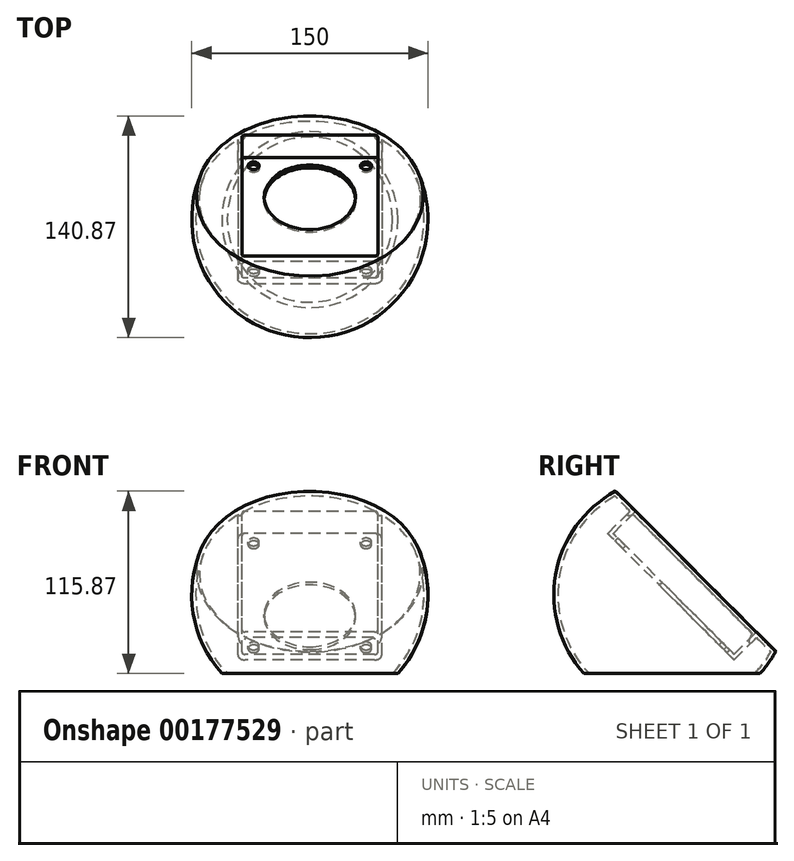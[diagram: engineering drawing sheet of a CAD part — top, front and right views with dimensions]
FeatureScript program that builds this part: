
annotation { "Feature Type Name" : "Feature", "Feature Type Description" : "" }
export const myFeature = defineFeature(function(context is Context, id is Id, definition is map)
    precondition{}
    {
        {
            var Q0;
            Q0=qCreatedBy(makeId("Front.planeOp"),FACE);
            var sketch = newSketch(context, id + "F0", { "sketchPlane" : qUnion([Q0])});
            skArc(sketch, "E0", {"start": v(55.9, 0) * mm, "mid": v(68.47, 80.62) * mm, "end": v(0, 125) * mm});
            skLineSegment(sketch, "E1", {"start": v(0, 0) * mm, "end": v(55.9, 0) * mm});
            skLineSegment(sketch, "E2", {"start": v(0, 50) * mm, "end": v(0, 0) * mm, "construction": true});
            skLineSegment(sketch, "E3", {"start": v(0, 0) * mm, "end": v(0, 125) * mm});
            skPoint(sketch, "E4.orphan", {"position": v(-55.9, 0) * mm});
            skSolve(sketch);
        }
        {
            var Q0;
            Q0=makeQuery(id+"F0.imprint","IMPRINT",FACE,{"disambiguationData":[TD([[makeQuery(id+"F0.imprint","IMPRINT",EDGE,{"derivedFrom":sQuery(id+"F0.wireOp",EDGE,"E0")}),1.0]])]});
            var Q1;
            Q1=sQuery(id+"F0.wireOp",EDGE,"E2");
            revolve(context, id + "F1", {"entities" : qUnion([Q0]), "axis" : qUnion([Q1]), "revolveType" : RevolveType.FULL});
        }
        {
            var Q0;
            Q0=makeQuery(id+"F1.opRevolve","SWEPT_FACE",FACE,{"disambiguationData":[OSD([sQuery(id+"F0.wireOp",EDGE,"E1")])]});
            var sketch = newSketch(context, id + "F2", { "sketchPlane" : qUnion([Q0])});
            skLineSegment(sketch, "E5", {"start": v(74.71, -80) * mm, "end": v(-64.99, -80) * mm, "construction": true});
            skSolve(sketch);
        }
        {
            var Q0;
            Q0=sQuery(id+"F2.wireOp",EDGE,"E5");
            cPlane(context, id + "F3", {"entities" : qUnion([Q0]), "cplaneType" : CPlaneType.LINE_ANGLE, "offset" : 25 * mm, "angle" : 45 * degree, "oppositeDirection" : true, "width" : 150 * mm, "height" : 150 * mm});
        }
        {
            var Q0;
            Q0=qCreatedBy(id+"F3.planeOp",FACE);
            var sketch = newSketch(context, id + "F4", { "sketchPlane" : qUnion([Q0])});
            skLineSegment(sketch, "E6.bottom", {"start": v(-80.9, 121.62) * mm, "end": v(80.9, 121.62) * mm});
            skLineSegment(sketch, "E6.top", {"start": v(-80.9, -121.62) * mm, "end": v(80.9, -121.62) * mm});
            skLineSegment(sketch, "E6.left", {"start": v(-80.9, 121.62) * mm, "end": v(-80.9, -121.62) * mm});
            skLineSegment(sketch, "E6.right", {"start": v(80.9, 121.62) * mm, "end": v(80.9, -121.62) * mm});
            skPoint(sketch, "E6.middle", {"position": v(0, 0) * mm});
            skSolve(sketch);
        }
        {
            var Q0;
            Q0=makeQuery(id+"F4.imprint","IMPRINT",FACE,{"disambiguationData":[TD([[makeQuery(id+"F4.imprint","IMPRINT",EDGE,{"derivedFrom":sQuery(id+"F4.wireOp",EDGE,"E6.bottom")}),-1.0]])]});
            extrude(context, id + "F5", {"entities" : qUnion([Q0]), "operationType" : NewBodyOperationType.REMOVE, "oppositeDirection" : true, "depth" : 100 * mm});
        }
        {
            var Q0;
            Q0=qCreatedBy(id+"F3.planeOp",FACE);
            var sketch = newSketch(context, id + "F6", { "sketchPlane" : qUnion([Q0])});
            skLineSegment(sketch, "E7.bottom", {"start": v(43.2, -17.25) * mm, "end": v(43.2, 87.25) * mm});
            skLineSegment(sketch, "E7.top", {"start": v(-43.2, -17.25) * mm, "end": v(-43.2, 87.25) * mm});
            skLineSegment(sketch, "E7.left", {"start": v(41.2, -19.25) * mm, "end": v(-41.2, -19.25) * mm});
            skLineSegment(sketch, "E7.right", {"start": v(41.2, 89.25) * mm, "end": v(-41.2, 89.25) * mm});
            skPoint(sketch, "E7.middle", {"position": v(0, 35) * mm});
            skPoint(sketch, "E8.visualSharp", {"position": v(-43.2, 89.25) * mm});
            skArc(sketch, "E8.filletArc", {"start": v(-41.2, 89.25) * mm, "mid": v(-42.61, 88.66) * mm, "end": v(-43.2, 87.25) * mm});
            skPoint(sketch, "E9.visualSharp", {"position": v(43.2, 89.25) * mm});
            skArc(sketch, "E9.filletArc", {"start": v(43.2, 87.25) * mm, "mid": v(42.61, 88.66) * mm, "end": v(41.2, 89.25) * mm});
            skPoint(sketch, "E10.visualSharp", {"position": v(43.2, -19.25) * mm});
            skArc(sketch, "E10.filletArc", {"start": v(41.2, -19.25) * mm, "mid": v(42.61, -18.66) * mm, "end": v(43.2, -17.25) * mm});
            skPoint(sketch, "E11.visualSharp", {"position": v(-43.2, -19.25) * mm});
            skArc(sketch, "E11.filletArc", {"start": v(-43.2, -17.25) * mm, "mid": v(-42.61, -18.66) * mm, "end": v(-41.2, -19.25) * mm});
            skCircle(sketch, "E12", {"center": v(0, 16.55) * mm, "radius": 29 * mm});
            skCircle(sketch, "E13", {"center": v(-35.7, 81.75) * mm, "radius": 3.5 * mm});
            skCircle(sketch, "E14", {"center": v(35.7, 81.75) * mm, "radius": 3.5 * mm});
            skCircle(sketch, "E15", {"center": v(35.7, -11.75) * mm, "radius": 3.5 * mm});
            skCircle(sketch, "E16", {"center": v(-35.7, -11.75) * mm, "radius": 3.5 * mm});
            skSolve(sketch);
        }
        {
            var Q0;
            Q0=makeQuery(id+"F6.imprint","IMPRINT",FACE,{"disambiguationData":[TD([[makeQuery(id+"F6.imprint","IMPRINT",EDGE,{"derivedFrom":sQuery(id+"F6.wireOp",EDGE,"E12")}),1.0]])]});
            var Q1;
            Q1=makeQuery(id+"F6.imprint","IMPRINT",FACE,{"disambiguationData":[TD([[makeQuery(id+"F6.imprint","IMPRINT",EDGE,{"derivedFrom":sQuery(id+"F6.wireOp",EDGE,"E13")}),1.0]])]});
            var Q2;
            Q2=makeQuery(id+"F6.imprint","IMPRINT",FACE,{"disambiguationData":[TD([[makeQuery(id+"F6.imprint","IMPRINT",EDGE,{"derivedFrom":sQuery(id+"F6.wireOp",EDGE,"E7.bottom")}),1.0]])]});
            var Q3;
            Q3=makeQuery(id+"F6.imprint","IMPRINT",FACE,{"disambiguationData":[TD([[makeQuery(id+"F6.imprint","IMPRINT",EDGE,{"derivedFrom":sQuery(id+"F6.wireOp",EDGE,"E14")}),1.0]])]});
            var Q4;
            Q4=makeQuery(id+"F6.imprint","IMPRINT",FACE,{"disambiguationData":[TD([[makeQuery(id+"F6.imprint","IMPRINT",EDGE,{"derivedFrom":sQuery(id+"F6.wireOp",EDGE,"E15")}),1.0]])]});
            var Q5;
            Q5=makeQuery(id+"F6.imprint","IMPRINT",FACE,{"disambiguationData":[TD([[makeQuery(id+"F6.imprint","IMPRINT",EDGE,{"derivedFrom":sQuery(id+"F6.wireOp",EDGE,"E16")}),1.0]])]});
            extrude(context, id + "F7", {"entities" : qUnion([Q0, Q1, Q2, Q3, Q4, Q5]), "operationType" : NewBodyOperationType.REMOVE, "depth" : 20 * mm});
        }
        {
            var Q0;
            Q0=makeQuery(id+"F1.opRevolve","SWEPT_FACE",FACE,{"disambiguationData":[OSD([sQuery(id+"F0.wireOp",EDGE,"E1")])]});
            shell(context, id + "F8", {"entities" : qUnion([Q0]), "thickness" : 2.5 * mm});
        }
        {
            var Q0;
            Q0=makeQuery(id+"F6.imprint","IMPRINT",FACE,{"disambiguationData":[TD([[makeQuery(id+"F6.imprint","IMPRINT",EDGE,{"derivedFrom":sQuery(id+"F6.wireOp",EDGE,"E12")}),1.0]])]});
            var Q1;
            Q1=makeQuery(id+"F6.imprint","IMPRINT",FACE,{"disambiguationData":[TD([[makeQuery(id+"F6.imprint","IMPRINT",EDGE,{"derivedFrom":sQuery(id+"F6.wireOp",EDGE,"E14")}),1.0]])]});
            var Q2;
            Q2=makeQuery(id+"F6.imprint","IMPRINT",FACE,{"disambiguationData":[TD([[makeQuery(id+"F6.imprint","IMPRINT",EDGE,{"derivedFrom":sQuery(id+"F6.wireOp",EDGE,"E16")}),1.0]])]});
            var Q3;
            Q3=makeQuery(id+"F6.imprint","IMPRINT",FACE,{"disambiguationData":[TD([[makeQuery(id+"F6.imprint","IMPRINT",EDGE,{"derivedFrom":sQuery(id+"F6.wireOp",EDGE,"E15")}),1.0]])]});
            var Q4;
            Q4=makeQuery(id+"F6.imprint","IMPRINT",FACE,{"disambiguationData":[TD([[makeQuery(id+"F6.imprint","IMPRINT",EDGE,{"derivedFrom":sQuery(id+"F6.wireOp",EDGE,"E13")}),1.0]])]});
            extrude(context, id + "F9", {"entities" : qUnion([Q0, Q1, Q2, Q3, Q4]), "operationType" : NewBodyOperationType.REMOVE, "depth" : 40 * mm});
        }
    });
